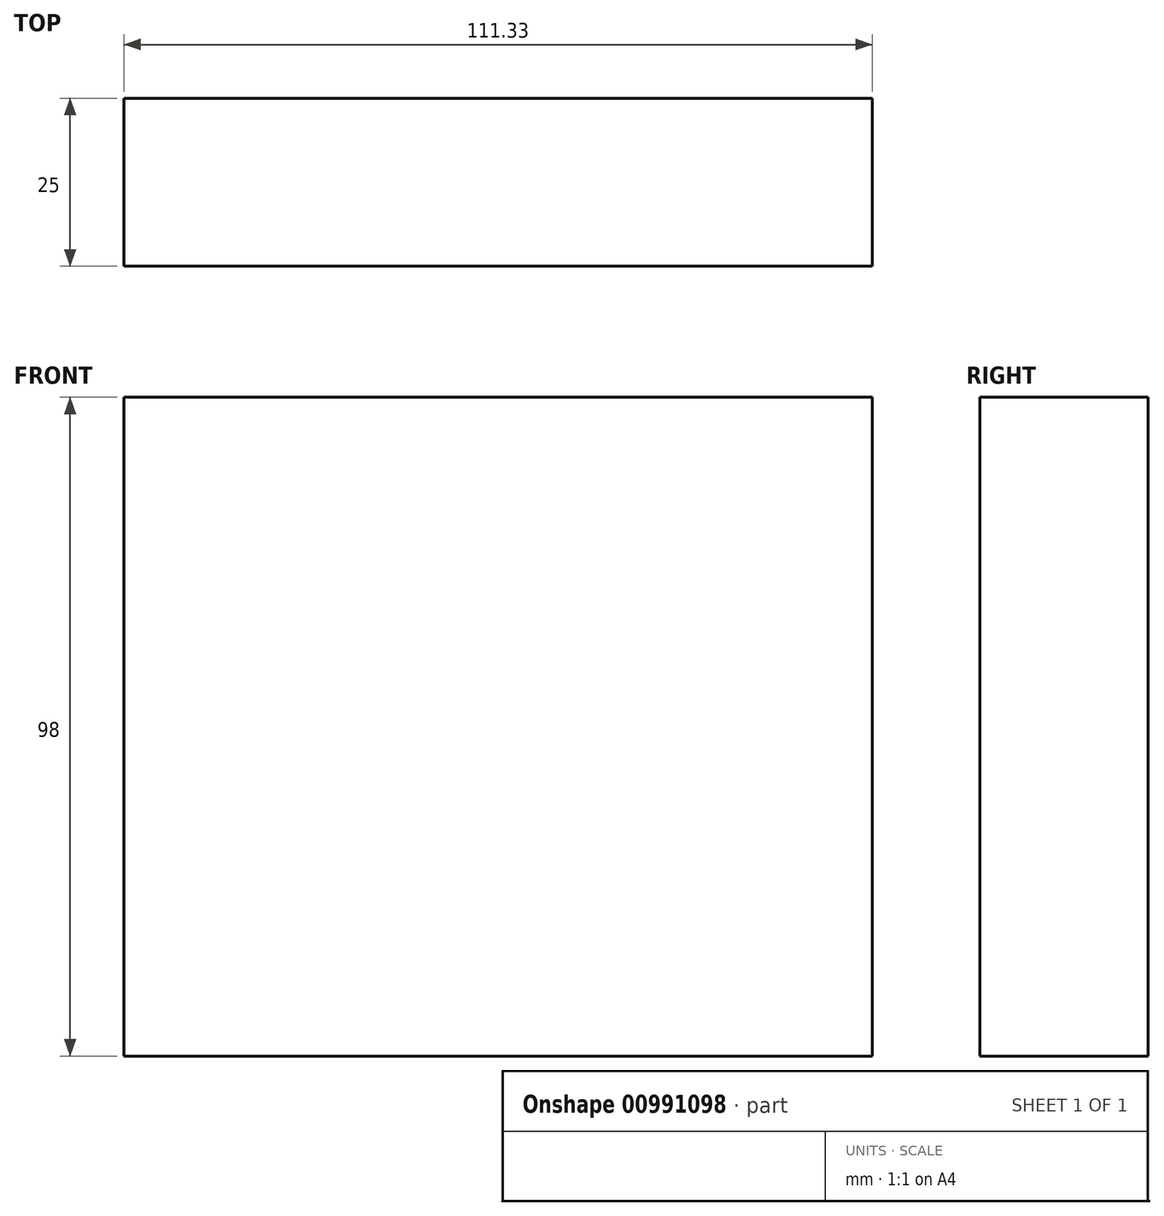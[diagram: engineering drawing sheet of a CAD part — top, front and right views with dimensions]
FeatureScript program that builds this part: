
annotation { "Feature Type Name" : "Feature", "Feature Type Description" : "" }
export const myFeature = defineFeature(function(context is Context, id is Id, definition is map)
    precondition{}
    {
        {
            var Q0;
            Q0=qCreatedBy(makeId("Front.planeOp"),FACE);
            var sketch = newSketch(context, id + "F0", { "sketchPlane" : qUnion([Q0])});
            skLineSegment(sketch, "E0.bottom", {"start": v(-51.7, 47.02) * mm, "end": v(59.63, 47.02) * mm});
            skLineSegment(sketch, "E0.top", {"start": v(-51.7, -50.98) * mm, "end": v(59.63, -50.98) * mm});
            skLineSegment(sketch, "E0.left", {"start": v(-51.7, 47.02) * mm, "end": v(-51.7, -50.98) * mm});
            skLineSegment(sketch, "E0.right", {"start": v(59.63, 47.02) * mm, "end": v(59.63, -50.98) * mm});
            skSolve(sketch);
        }
        {
            var Q0;
            Q0=makeQuery(id+"F0.imprint","IMPRINT",FACE,{"disambiguationData":[TD([[makeQuery(id+"F0.imprint","IMPRINT",EDGE,{"derivedFrom":sQuery(id+"F0.wireOp",EDGE,"E0.bottom")}),-1.0]])]});
            extrude(context, id + "F1", {"entities" : qUnion([Q0]), "depth" : 25 * mm, "offsetDistance" : 25 * mm});
        }
    });
